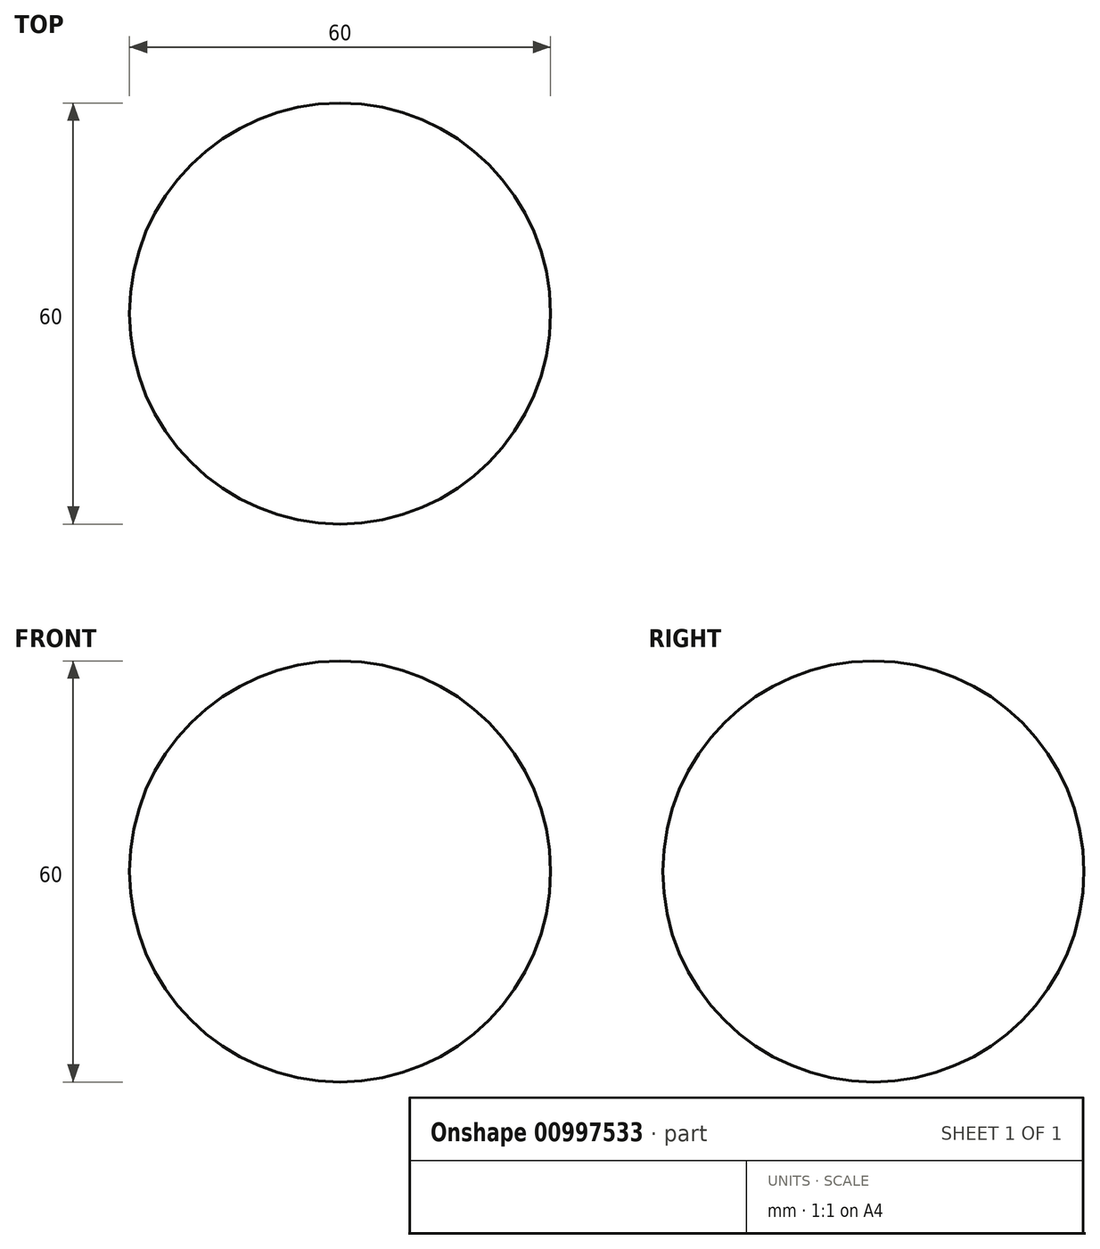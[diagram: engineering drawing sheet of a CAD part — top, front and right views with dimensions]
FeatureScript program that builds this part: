
annotation { "Feature Type Name" : "Feature", "Feature Type Description" : "" }
export const myFeature = defineFeature(function(context is Context, id is Id, definition is map)
    precondition{}
    {
        {
            var Q0;
            Q0=qCreatedBy(makeId("Front.planeOp"),FACE);
            var sketch = newSketch(context, id + "F0", { "sketchPlane" : qUnion([Q0])});
            skCircle(sketch, "E0", {"center": v(0, 0) * mm, "radius": 30 * mm});
            skLineSegment(sketch, "E1", {"start": v(0, -30) * mm, "end": v(0, 30) * mm});
            skSolve(sketch);
        }
        {
            var Q0;
            {var subQ0=sQuery(id+"F0.wireOp",EDGE,"E1");Q0=makeQuery(id+"F0.imprint","IMPRINT",FACE,{"disambiguationData":[TD([[makeQuery(id+"F0.imprint","IMPRINT",EDGE,{"derivedFrom":subQ0}),1.0]])]});}
            var Q1;
            Q1=sQuery(id+"F0.wireOp",EDGE,"E1");
            revolve(context, id + "F1", {"surfaceOperationType" : NewSurfaceOperationType.NEW, "entities" : qUnion([Q0]), "axis" : qUnion([Q1]), "revolveType" : RevolveType.FULL});
        }
    });
